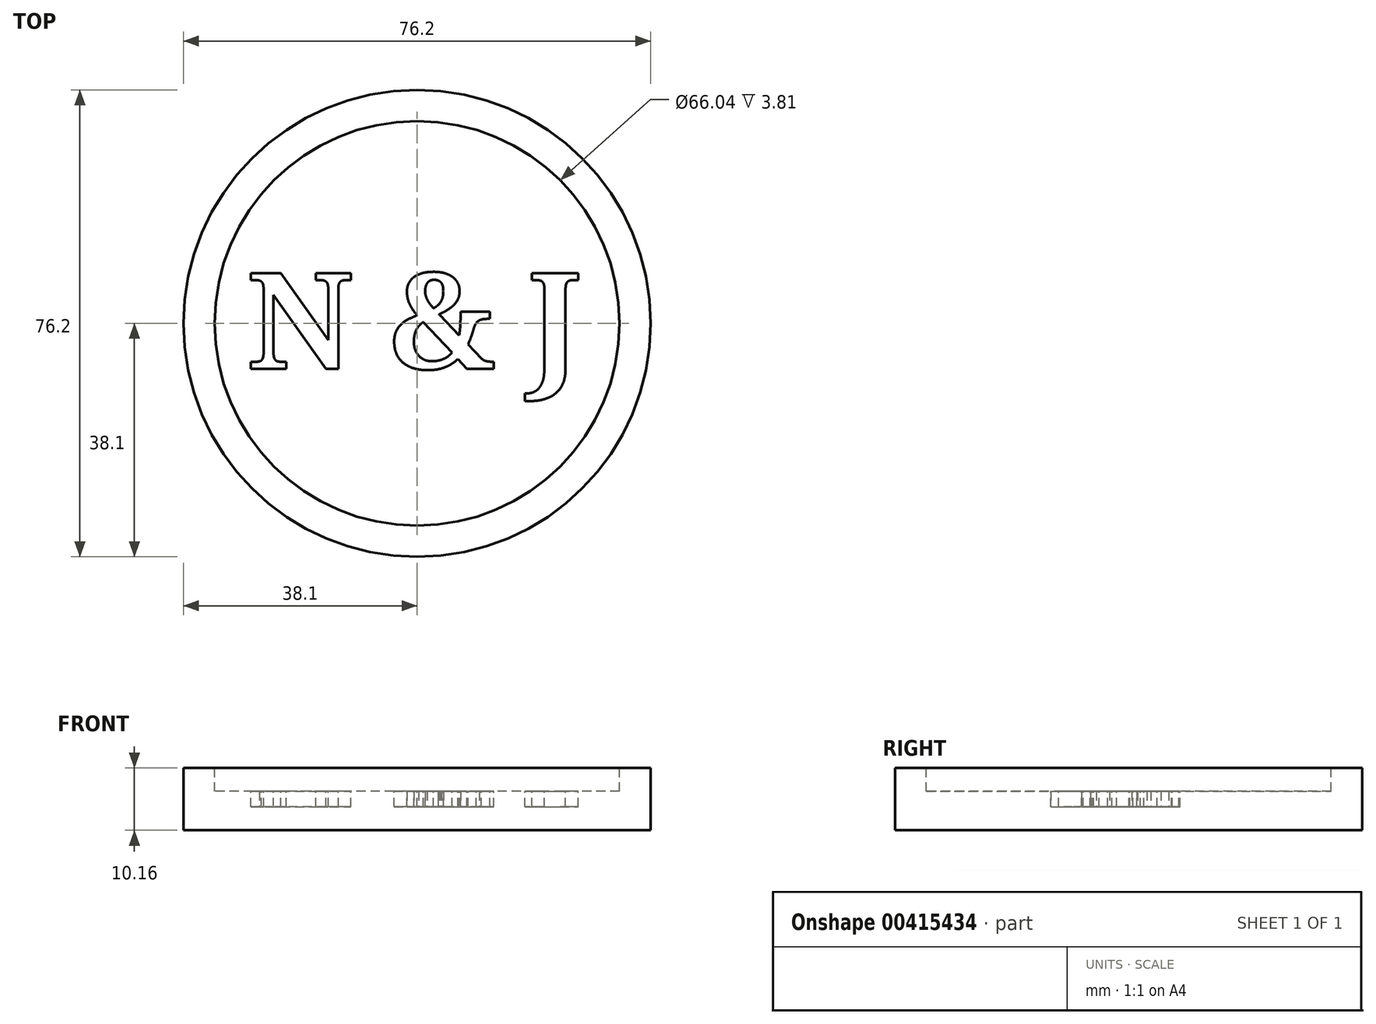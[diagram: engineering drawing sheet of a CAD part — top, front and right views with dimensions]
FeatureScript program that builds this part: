
annotation { "Feature Type Name" : "Feature", "Feature Type Description" : "" }
export const myFeature = defineFeature(function(context is Context, id is Id, definition is map)
    precondition{}
    {
        {
            var Q0;
            Q0=qCreatedBy(makeId("Top.planeOp"),FACE);
            var sketch = newSketch(context, id + "F0", { "sketchPlane" : qUnion([Q0])});
            skCircle(sketch, "E0", {"center": v(0, 0) * mm, "radius": 38.1 * mm});
            skSolve(sketch);
        }
        {
            var Q0;
            Q0=makeQuery(id+"F0.imprint","IMPRINT",FACE,{"disambiguationData":[TD([[makeQuery(id+"F0.imprint","IMPRINT",EDGE,{"derivedFrom":sQuery(id+"F0.wireOp",EDGE,"E0")}),1.0]])]});
            extrude(context, id + "F1", {"entities" : qUnion([Q0]), "depth" : 10.16 * mm});
        }
        {
            var Q0;
            Q0=makeQuery(id+"F1.opExtrude","CAP_FACE",FACE,{"disambiguationData":[OSD([sQuery(id+"F0.wireOp",EDGE,"E0")])],"isStart":false});
            var sketch = newSketch(context, id + "F2", { "sketchPlane" : qUnion([Q0])});
            skCircle(sketch, "E1", {"center": v(0, 0) * mm, "radius": 33.02 * mm});
            skSolve(sketch);
        }
        {
            var Q0;
            Q0=makeQuery(id+"F2.imprint","IMPRINT",FACE,{"disambiguationData":[TD([[makeQuery(id+"F2.imprint","IMPRINT",EDGE,{"derivedFrom":sQuery(id+"F2.wireOp",EDGE,"E1")}),1.0]])]});
            extrude(context, id + "F3", {"entities" : qUnion([Q0]), "operationType" : NewBodyOperationType.REMOVE, "oppositeDirection" : true, "depth" : 3.8 * mm});
        }
        {
            var Q0;
            Q0=makeQuery(id+"F3.boolean.opBoolean","COPY",FACE,{"derivedFrom":makeQuery(id+"F3.opExtrude","CAP_FACE",FACE,{"disambiguationData":[OSD([sQuery(id+"F2.wireOp",EDGE,"E1")])],"isStart":false})});
            var sketch = newSketch(context, id + "F4", { "sketchPlane" : qUnion([Q0])});
            skText(sketch, "E2", { "text": "N & J", "fontName": "NotoSerif-Bold.ttf"});
            const initialGuessF4  = {"E2": [-0.0277, -0.00743, 1, 0, 0.01576]};
            skSetInitialGuess(sketch, initialGuessF4);
            skSolve(sketch);
        }
        {
            var Q0;
            Q0 = qSketchRegion(id + "F4", true);
            extrude(context, id + "F5", {"entities" : qUnion([Q0]), "operationType" : NewBodyOperationType.REMOVE, "oppositeDirection" : true, "depth" : 2.54 * mm});
        }
    });
